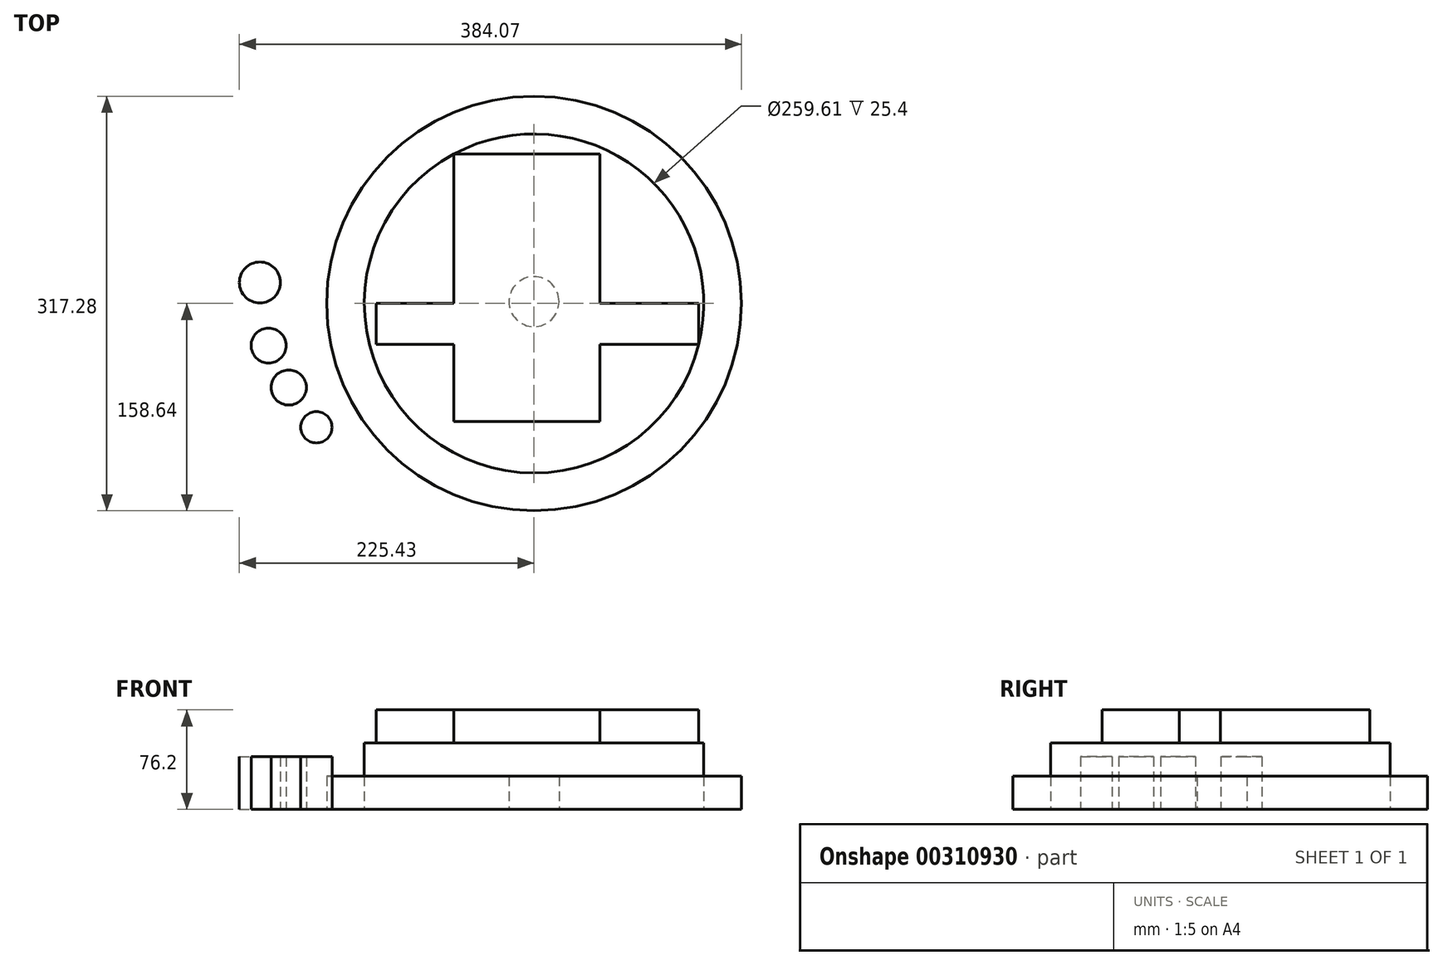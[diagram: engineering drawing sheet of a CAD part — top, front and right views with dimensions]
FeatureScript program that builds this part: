
annotation { "Feature Type Name" : "Feature", "Feature Type Description" : "" }
export const myFeature = defineFeature(function(context is Context, id is Id, definition is map)
    precondition{}
    {
        {
            var Q0;
            Q0=qCreatedBy(makeId("Top.planeOp"),FACE);
            var sketch = newSketch(context, id + "F0", { "sketchPlane" : qUnion([Q0])});
            skCircle(sketch, "E0", {"center": v(0, 0) * mm, "radius": 158.64 * mm});
            skCircle(sketch, "E1", {"center": v(0, 0) * mm, "radius": 129.8 * mm});
            skCircle(sketch, "E2", {"center": v(0, 1.4) * mm, "radius": 19.13 * mm});
            skSolve(sketch);
        }
        {
            var Q0;
            Q0=makeQuery(id+"F0.imprint","IMPRINT",FACE,{"disambiguationData":[TD([[makeQuery(id+"F0.imprint","IMPRINT",EDGE,{"derivedFrom":sQuery(id+"F0.wireOp",EDGE,"E0")}),1.0]])]});
            var Q1;
            Q1=makeQuery(id+"F0.imprint","IMPRINT",FACE,{"disambiguationData":[TD([[makeQuery(id+"F0.imprint","IMPRINT",EDGE,{"derivedFrom":sQuery(id+"F0.wireOp",EDGE,"E2")}),1.0]])]});
            extrude(context, id + "F1", {"entities" : qUnion([Q0, Q1]), "depth" : 25.4 * mm});
        }
        {
            var Q0;
            Q0=makeQuery(id+"F1.opExtrude","CAP_FACE",FACE,{"disambiguationData":[OSD([sQuery(id+"F0.wireOp",EDGE,"E0"),sQuery(id+"F0.wireOp",EDGE,"E1")])],"isStart":false});
            var sketch = newSketch(context, id + "F2", { "sketchPlane" : qUnion([Q0])});
            skLineSegment(sketch, "E3.bottom", {"start": v(-51.15, -187.93) * mm, "end": v(0, -187.93) * mm, "construction": true});
            skLineSegment(sketch, "E3.top", {"start": v(-51.15, -158.64) * mm, "end": v(0, -158.64) * mm});
            skLineSegment(sketch, "E3.left", {"start": v(-51.15, -187.93) * mm, "end": v(-51.15, -158.64) * mm});
            skLineSegment(sketch, "E3.right", {"start": v(0, -187.93) * mm, "end": v(0, -158.64) * mm});
            skSolve(sketch);
        }
        {
            var Q0;
            Q0=makeQuery(id+"F1.opExtrude","CAP_FACE",FACE,{"disambiguationData":[OSD([sQuery(id+"F0.wireOp",EDGE,"E0"),sQuery(id+"F0.wireOp",EDGE,"E1")])],"isStart":true});
            var sketch = newSketch(context, id + "F3", { "sketchPlane" : qUnion([Q0])});
            skCircle(sketch, "E4", {"center": v(-209.7, -16.02) * mm, "radius": 15.73 * mm});
            skCircle(sketch, "E5", {"center": v(-203.06, 32.24) * mm, "radius": 13.36 * mm});
            skCircle(sketch, "E6", {"center": v(-187.62, 64.35) * mm, "radius": 13.45 * mm});
            skCircle(sketch, "E7", {"center": v(-166.5, 94.78) * mm, "radius": 12 * mm});
            skSolve(sketch);
        }
        {
            var Q0;
            Q0 = qSketchRegion(id + "F3", true);
            extrude(context, id + "F4", {"entities" : qUnion([Q0]), "oppositeDirection" : true, "depth" : 40.4 * mm});
        }
        {
            var Q0;
            Q0=makeQuery(id+"F2.imprint","IMPRINT",FACE,{"disambiguationData":[TD([[makeQuery(id+"F2.imprint","IMPRINT",EDGE,{"derivedFrom":makeQuery(id+"F1.opExtrude","CAP_EDGE",EDGE,{"disambiguationData":[OSD([sQuery(id+"F0.wireOp",EDGE,"E1")])],"isStart":false})}),1.0]])]});
            var sketch = newSketch(context, id + "F5", { "sketchPlane" : qUnion([Q0])});
            skLineSegment(sketch, "E8.bottom", {"start": v(24.96, 0) * mm, "end": v(119.1, 0) * mm});
            skLineSegment(sketch, "E8.top", {"start": v(24.96, -13.72) * mm, "end": v(119.1, -13.72) * mm});
            skLineSegment(sketch, "E8.left", {"start": v(24.96, 0) * mm, "end": v(24.96, -13.72) * mm});
            skLineSegment(sketch, "E8.right", {"start": v(119.1, 0) * mm, "end": v(119.1, -13.72) * mm});
            skLineSegment(sketch, "E9.bottom", {"start": v(-15.34, -6.31) * mm, "end": v(-86.15, -6.31) * mm});
            skLineSegment(sketch, "E9.top", {"start": v(-15.34, 8.98) * mm, "end": v(-86.15, 8.98) * mm});
            skLineSegment(sketch, "E9.left", {"start": v(-15.34, -6.31) * mm, "end": v(-15.34, 8.98) * mm});
            skLineSegment(sketch, "E9.right", {"start": v(-86.15, -6.31) * mm, "end": v(-86.15, 8.98) * mm});
            skLineSegment(sketch, "E10.bottom", {"start": v(0, 18.73) * mm, "end": v(-19.37, 18.73) * mm});
            skLineSegment(sketch, "E10.top", {"start": v(0, 75.02) * mm, "end": v(-19.37, 75.02) * mm});
            skLineSegment(sketch, "E10.left", {"start": v(0, 18.73) * mm, "end": v(0, 75.02) * mm});
            skLineSegment(sketch, "E10.right", {"start": v(-19.37, 18.73) * mm, "end": v(-19.37, 75.02) * mm});
            skPoint(sketch, "E11.firstSnap0", {"position": v(0, 46.87) * mm});
            skPoint(sketch, "E11.oppositeSnap0", {"position": v(24.96, -6.86) * mm});
            skLineSegment(sketch, "E11.bottom", {"start": v(0, -13.72) * mm, "end": v(24.96, -13.72) * mm});
            skLineSegment(sketch, "E11.top", {"start": v(0, -79.26) * mm, "end": v(24.96, -79.26) * mm});
            skLineSegment(sketch, "E11.left", {"start": v(0, -13.72) * mm, "end": v(0, -79.26) * mm});
            skLineSegment(sketch, "E11.right", {"start": v(24.96, -13.72) * mm, "end": v(24.96, -79.26) * mm});
            skSolve(sketch);
        }
        {
            var Q0;
            Q0=makeQuery(id+"F5.imprint","IMPRINT",FACE,{"disambiguationData":[TD([[makeQuery(id+"F5.imprint","IMPRINT",EDGE,{"derivedFrom":sQuery(id+"F5.wireOp",EDGE,"E8.bottom")}),-1.0]])]});
            var Q1;
            Q1=makeQuery(id+"F5.imprint","IMPRINT",FACE,{"disambiguationData":[TD([[makeQuery(id+"F5.imprint","IMPRINT",EDGE,{"derivedFrom":sQuery(id+"F5.wireOp",EDGE,"E11.bottom")}),-1.0]])]});
            var Q2;
            Q2=makeQuery(id+"F5.imprint","IMPRINT",FACE,{"disambiguationData":[TD([[makeQuery(id+"F5.imprint","IMPRINT",EDGE,{"derivedFrom":sQuery(id+"F5.wireOp",EDGE,"E10.bottom")}),-1.0]])]});
            var Q3;
            Q3=makeQuery(id+"F2.imprint","IMPRINT",FACE,{"disambiguationData":[TD([[makeQuery(id+"F2.imprint","IMPRINT",EDGE,{"derivedFrom":makeQuery(id+"F1.opExtrude","CAP_EDGE",EDGE,{"disambiguationData":[OSD([sQuery(id+"F0.wireOp",EDGE,"E1")])],"isStart":false})}),1.0]])]});
            extrude(context, id + "F6", {"entities" : qUnion([Q0, Q1, Q2, Q3]), "operationType" : NewBodyOperationType.ADD, "depth" : 25.4 * mm});
        }
        {
            var Q0;
            Q0=makeQuery(id+"F6.opExtrude","CAP_FACE",FACE,{"disambiguationData":[OSD([sQuery(id+"F0.wireOp",EDGE,"E1")])],"isStart":false});
            var sketch = newSketch(context, id + "F7", { "sketchPlane" : qUnion([Q0])});
            skLineSegment(sketch, "E12.bottom", {"start": v(-120.86, 0) * mm, "end": v(125.94, 0) * mm});
            skLineSegment(sketch, "E12.top", {"start": v(-120.86, -31.46) * mm, "end": v(125.94, -31.46) * mm});
            skLineSegment(sketch, "E12.left", {"start": v(-120.86, 0) * mm, "end": v(-120.86, -31.46) * mm});
            skLineSegment(sketch, "E12.right", {"start": v(125.94, 0) * mm, "end": v(125.94, -31.46) * mm});
            skLineSegment(sketch, "E13.bottom", {"start": v(50.53, -90.26) * mm, "end": v(-61.22, -90.26) * mm});
            skLineSegment(sketch, "E13.top", {"start": v(50.53, 114.47) * mm, "end": v(-61.22, 114.47) * mm});
            skLineSegment(sketch, "E13.left", {"start": v(50.53, -90.26) * mm, "end": v(50.53, 114.47) * mm});
            skLineSegment(sketch, "E13.right", {"start": v(-61.22, -90.26) * mm, "end": v(-61.22, 114.47) * mm});
            skSolve(sketch);
        }
        {
            var Q0;
            Q0 = qSketchRegion(id + "F7", true);
            extrude(context, id + "F8", {"entities" : qUnion([Q0]), "operationType" : NewBodyOperationType.ADD, "depth" : 25.4 * mm});
        }
    });
